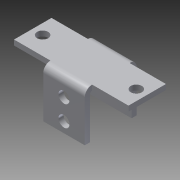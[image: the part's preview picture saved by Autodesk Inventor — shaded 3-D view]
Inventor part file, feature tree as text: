
AUTODESK INVENTOR PART (.ipt)
format: ipt  version: 2013 (Build 170138000, 138)  size: 172,032 bytes
history: native  units: in
note: dims shown in document units (in); Inventor stores cm internally (conversion verified against a paired STEP export)
features: sheet_metal_op x9, sketch x6, other x5, reference x2, extrude x1
ambient origin geometry x8: Origin, YZ Plane, XZ Plane, XY Plane, X Axis, Y Axis, Z Axis, Center Point
bodies: Solid1 (feature_tree)
feature tree (23):
  sheet_metal_op  "Face1"
  sheet_metal_op  "Flange1"
  sketch  "Sketch3"  dims[d3=0.125in]
  sheet_metal_op  "Flange2"
  extrude  "Extrusion1"  Depth=1.0in
  sheet_metal_op  "Face2"
  sketch  "Sketch1"  dims[d0=1.0in d1=1.0in]
  other  "Plate1"
  sketch  "Sketch2"  dims[d2=0.125in]
  other  "Plate2"
  sheet_metal_op  "Bend1"
  sheet_metal_op  "Corner1"
  sketch  "Sketch4"  dims[d4=0.0625in]
  other  "Plate3"
  sheet_metal_op  "Bend2"
  sheet_metal_op  "Corner2"
  sketch  "Sketch5"  dims[d5=0.25in]
  other  "Plate4"
  sheet_metal_op  "Bend3"
  sketch  "Sketch6"  dims[d6=0.125in d7=1.075in d8=90.0deg d9=0.05in d10=0.5in d11=0.125in d12=0.125in d13=0.25in d14=0.25in d15=0.25in d16=0.266in d17=0.266in d18=0.125in d19=0.0625in d20=0.25in d21=0.125in d22=1.175in d23=90.0deg d24=0.05in d25=0.5in d26=0.125in d27=0.125in d28=1.5in d29=0.0in d30=0.875in d31=0.9in d32=0.875in d33=0.05in d34=0.125in d35=0.0625in d36=0.25in d37=0.125in d38=0.125in d39=0.0in]
  reference  "Reference1"
  reference  "Reference2"
  other  "Cut1"
